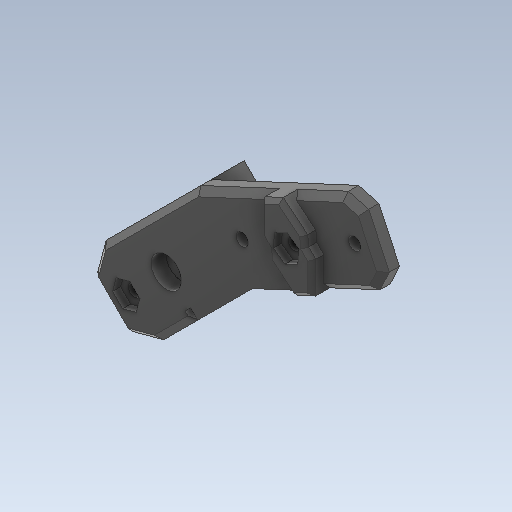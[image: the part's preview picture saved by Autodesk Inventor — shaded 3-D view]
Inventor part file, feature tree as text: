
AUTODESK INVENTOR PART (.ipt)
format: ipt  version: 2020 (Build 240168000, 168)  size: 284,672 bytes
history: native  units: in
note: dims shown in document units (in); Inventor stores cm internally (conversion verified against a paired STEP export)
features: sketch x13, other x3
ambient origin geometry x8: Origin, YZ Plane, XZ Plane, XY Plane, X Axis, Y Axis, Z Axis, Center Point
bodies: Solid1 (feature_tree)
feature tree (16):
  other  "TibiaBot.ipt"
  other  "Solid1::TibiaBot.ipt"
  other  "TaggingFeature1"
  sketch  "Sketch1"  dims[d0=0.3937in]
  sketch  "Sketch9"
  sketch  "Sketch10"
  sketch  "Sketch11"
  sketch  "Sketch15"
  sketch  "Sketch25"
  sketch  "Sketch26"
  sketch  "Sketch8"
  sketch  "Sketch12"
  sketch  "Sketch13"
  sketch  "Sketch19"
  sketch  "Sketch20"
  sketch  "Sketch21"
